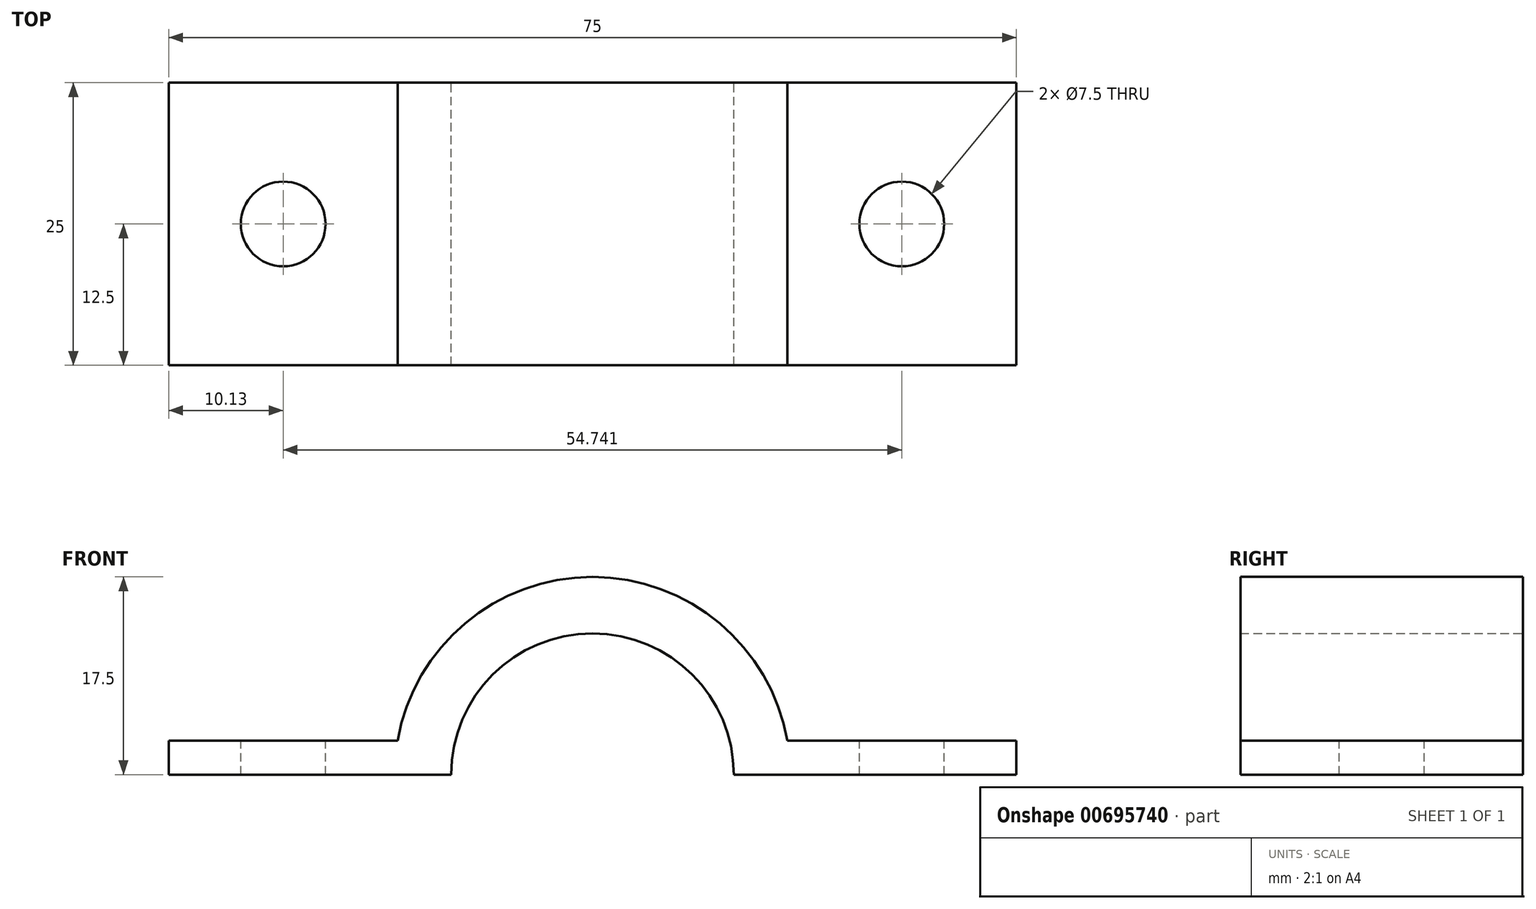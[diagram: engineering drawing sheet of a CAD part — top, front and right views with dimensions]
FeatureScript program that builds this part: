
annotation { "Feature Type Name" : "Feature", "Feature Type Description" : "" }
export const myFeature = defineFeature(function(context is Context, id is Id, definition is map)
    precondition{}
    {
        {
            var Q0;
            Q0=qCreatedBy(makeId("Front.planeOp"),FACE);
            var sketch = newSketch(context, id + "F0", { "sketchPlane" : qUnion([Q0])});
            skArc(sketch, "E0", {"start": v(12.5, 0) * mm, "mid": v(0, 12.5) * mm, "end": v(-12.5, 0) * mm});
            skArc(sketch, "E1", {"start": v(17.24, 3) * mm, "mid": v(0, 17.5) * mm, "end": v(-17.24, 3) * mm});
            skLineSegment(sketch, "E2", {"start": v(-17.5, 0) * mm, "end": v(-37.5, 0) * mm});
            skLineSegment(sketch, "E3", {"start": v(-37.5, 0) * mm, "end": v(-37.5, 3) * mm});
            skLineSegment(sketch, "E4", {"start": v(-37.5, 3) * mm, "end": v(-17.24, 3) * mm});
            skLineSegment(sketch, "E5", {"start": v(17.5, 0) * mm, "end": v(37.5, 0) * mm});
            skLineSegment(sketch, "E6", {"start": v(37.5, 0) * mm, "end": v(37.5, 3) * mm});
            skLineSegment(sketch, "E7", {"start": v(37.5, 3) * mm, "end": v(17.24, 3) * mm});
            skLineSegment(sketch, "E8", {"start": v(-17.5, 0) * mm, "end": v(-12.5, 0) * mm});
            skLineSegment(sketch, "E9", {"start": v(12.5, 0) * mm, "end": v(17.5, 0) * mm});
            skSolve(sketch);
        }
        {
            var Q0;
            Q0 = qSketchRegion(id + "F0", true);
            extrude(context, id + "F1", {"entities" : qUnion([Q0]), "depth" : 25 * mm, "offsetDistance" : 25 * mm});
        }
        {
            var Q0;
            Q0=makeQuery(id+"F1.opExtrude","SWEPT_FACE",FACE,{"disambiguationData":[OSD([sQuery(id+"F0.wireOp",EDGE,"E4")])]});
            var sketch = newSketch(context, id + "F2", { "sketchPlane" : qUnion([Q0])});
            skLineSegment(sketch, "E10.0.0", {"start": v(37.5, 0) * mm, "end": v(17.24, 0) * mm});
            skLineSegment(sketch, "E10.0.1", {"start": v(17.24, 0) * mm, "end": v(17.24, -25) * mm});
            skLineSegment(sketch, "E10.0.2", {"start": v(17.24, -25) * mm, "end": v(37.5, -25) * mm});
            skLineSegment(sketch, "E10.0.3", {"start": v(37.5, -25) * mm, "end": v(37.5, 0) * mm});
            skPoint(sketch, "E11", {"position": v(-27.37, -12.5) * mm});
            skPoint(sketch, "E11.positionSnap0", {"position": v(-27.37, 0) * mm});
            skPoint(sketch, "E11.positionSnap1", {"position": v(-37.5, -12.5) * mm});
            skPoint(sketch, "E12", {"position": v(27.37, -12.5) * mm});
            skPoint(sketch, "E12.positionSnap0", {"position": v(37.5, -12.5) * mm});
            skPoint(sketch, "E12.positionSnap1", {"position": v(27.37, 0) * mm});
            skSolve(sketch);
        }
        {
            var Q0;
            Q0=sQuery(id+"F2.wireOp",VERTEX,"E11");
            var Q1;
            Q1=makeQuery(id+"F1.opExtrude","SWEPT_BODY",BODY,{"disambiguationData":[OSD([sQuery(id+"F0.wireOp",EDGE,"E0"),sQuery(id+"F0.wireOp",EDGE,"E1"),sQuery(id+"F0.wireOp",EDGE,"E2"),sQuery(id+"F0.wireOp",EDGE,"E3"),sQuery(id+"F0.wireOp",EDGE,"E4"),sQuery(id+"F0.wireOp",EDGE,"E5"),sQuery(id+"F0.wireOp",EDGE,"E6"),sQuery(id+"F0.wireOp",EDGE,"E7"),sQuery(id+"F0.wireOp",EDGE,"E8"),sQuery(id+"F0.wireOp",EDGE,"E9")])]});
            hole(context, id + "F3", {"style" : HoleStyle.SIMPLE, "endStyle" : HoleEndStyle.THROUGH, "holeDiameter" : 7.5 * mm, "majorDiameter" : 5 * mm, "isTappedThrough" : true, "tappedDepth" : 12 * mm, "tapClearance" : 3, "locations" : qUnion([Q0]), "scope" : qUnion([Q1])});
        }
        {
            var Q0;
            Q0=sQuery(id+"F2.wireOp",VERTEX,"E12");
            var Q1;
            Q1=makeQuery(id+"F1.opExtrude","SWEPT_BODY",BODY,{"disambiguationData":[OSD([sQuery(id+"F0.wireOp",EDGE,"E0"),sQuery(id+"F0.wireOp",EDGE,"E1"),sQuery(id+"F0.wireOp",EDGE,"E2"),sQuery(id+"F0.wireOp",EDGE,"E3"),sQuery(id+"F0.wireOp",EDGE,"E4"),sQuery(id+"F0.wireOp",EDGE,"E5"),sQuery(id+"F0.wireOp",EDGE,"E6"),sQuery(id+"F0.wireOp",EDGE,"E7"),sQuery(id+"F0.wireOp",EDGE,"E8"),sQuery(id+"F0.wireOp",EDGE,"E9")])]});
            hole(context, id + "F4", {"style" : HoleStyle.SIMPLE, "endStyle" : HoleEndStyle.THROUGH, "holeDiameter" : 7.5 * mm, "majorDiameter" : 5 * mm, "isTappedThrough" : true, "tappedDepth" : 12 * mm, "tapClearance" : 3, "locations" : qUnion([Q0]), "scope" : qUnion([Q1])});
        }
    });
